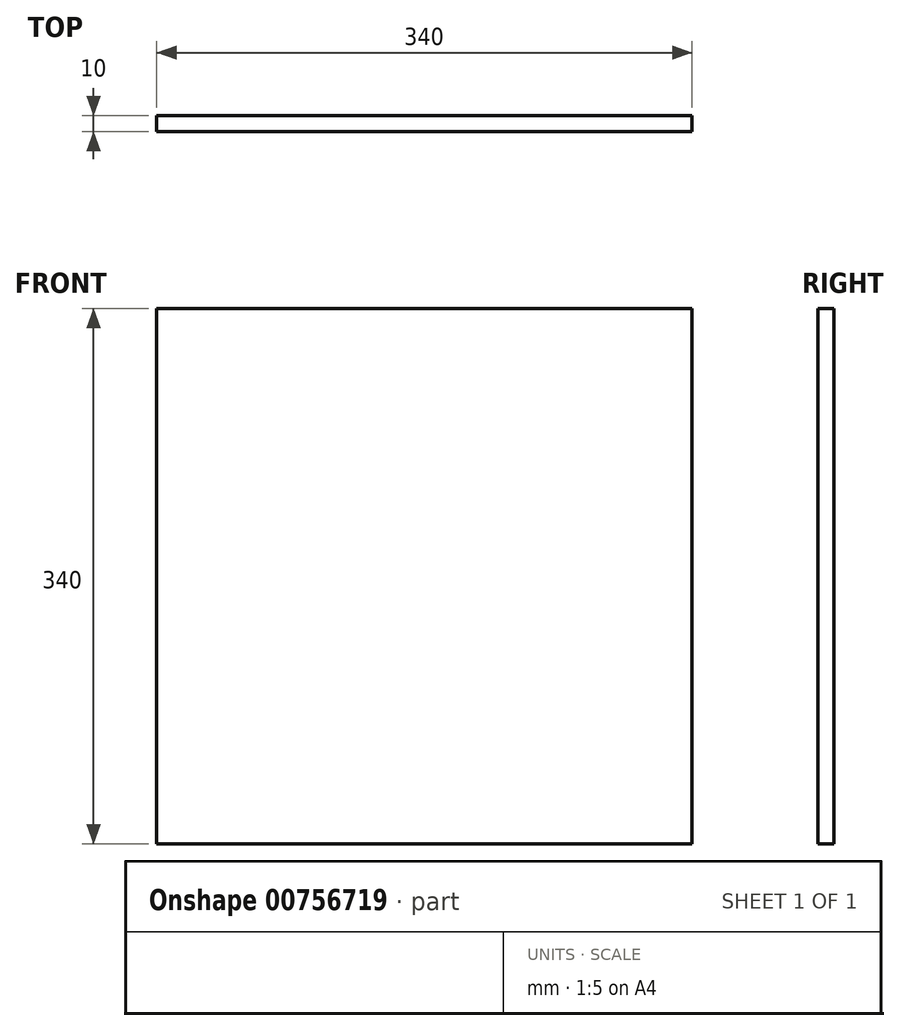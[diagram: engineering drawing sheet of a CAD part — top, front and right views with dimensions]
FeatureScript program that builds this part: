
annotation { "Feature Type Name" : "Feature", "Feature Type Description" : "" }
export const myFeature = defineFeature(function(context is Context, id is Id, definition is map)
    precondition{}
    {
        {
            var Q0;
            Q0=qCreatedBy(makeId("Front.planeOp"),FACE);
            var sketch = newSketch(context, id + "F0", { "sketchPlane" : qUnion([Q0])});
            skLineSegment(sketch, "E0.bottom", {"start": v(0, 0) * mm, "end": v(340, 0) * mm});
            skLineSegment(sketch, "E0.top", {"start": v(0, -340) * mm, "end": v(340, -340) * mm});
            skLineSegment(sketch, "E0.left", {"start": v(0, 0) * mm, "end": v(0, -340) * mm});
            skLineSegment(sketch, "E0.right", {"start": v(340, 0) * mm, "end": v(340, -340) * mm});
            skSolve(sketch);
        }
        {
            var Q0;
            Q0=makeQuery(id+"F0.imprint","IMPRINT",FACE,{"disambiguationData":[TD([[makeQuery(id+"F0.imprint","IMPRINT",EDGE,{"derivedFrom":sQuery(id+"F0.wireOp",EDGE,"E0.bottom")}),-1.0]])]});
            extrude(context, id + "F1", {"entities" : qUnion([Q0]), "depth" : 10 * mm, "offsetDistance" : 25 * mm});
        }
    });
